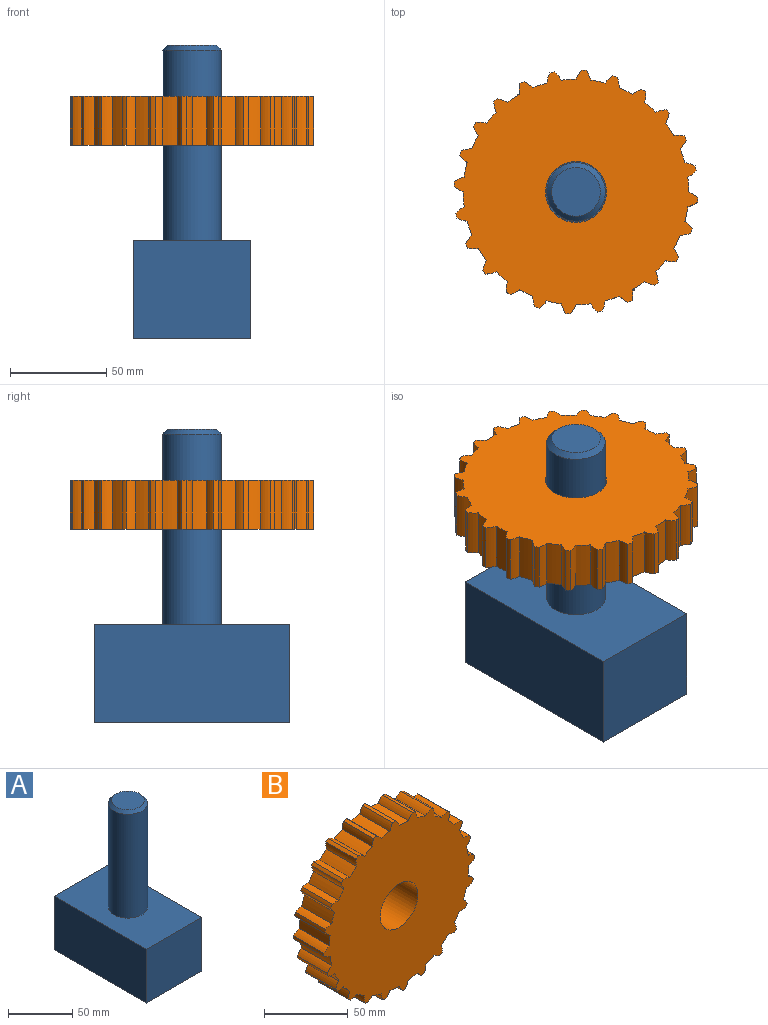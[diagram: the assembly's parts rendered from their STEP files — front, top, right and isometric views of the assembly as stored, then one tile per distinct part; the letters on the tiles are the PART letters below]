
ASSEMBLY  parts=2 mates=1
PART A: 9 faces, bbox 61.1x101.6x152.8 mm
  f0: plane 101.6x51.17mm, normal (1,0,0), area 5198.7mm2, adj f1,f3,f4,f5
  f1: plane 101.6x61.1mm, normal (0,0,1), area 5478.3mm2, adj f0,f2,f4,f5,f6
  f2: plane 101.6x51.17mm, normal (-1,0,0), area 5198.7mm2, adj f1,f3,f4,f5
  f3: plane 101.6x61.1mm, normal (0,0,-1), area 6207.9mm2, adj f0,f2,f4,f5
  f4: plane 61.1x51.17mm, normal (0,-1,0), area 3126.5mm2, adj f0,f1,f2,f3
  f5: plane 61.1x51.17mm, normal (0,1,0), area 3126.5mm2, adj f0,f1,f2,f3
  f6: cylinder r=15.24mm len=99.06mm, axis (0,0,-1), area 9485.6mm2, adj f1,f8
  f7: plane 25.4x25.4mm, normal (0,0,1), area 506.7mm2, adj f8
  f8: cone r=12.7mm half-angle=45deg, axis (0,0,-1), area 315.3mm2, adj f6,f7
PART B: 99 faces, bbox 126.7x25.4x126.7 mm
  f0: cylinder r=14.67mm len=25.4mm, axis (0,1,0), area 141.4mm2, adj f23,f26,f27,f28
  f1: cylinder r=58.67mm len=25.4mm, axis (0,1,0), area 195.1mm2, adj f27,f28,f68,f71
  f2: cylinder r=58.67mm len=25.4mm, axis (0,1,0), area 195.1mm2, adj f27,f28,f65,f67
  f3: cylinder r=58.67mm len=25.4mm, axis (0,1,0), area 195.1mm2, adj f27,f28,f62,f64
  f4: cylinder r=58.67mm len=25.4mm, axis (0,1,0), area 195.1mm2, adj f27,f28,f70,f74
  f5: cylinder r=58.67mm len=25.4mm, axis (0,1,0), area 195.1mm2, adj f27,f28,f73,f77
  f6: cylinder r=58.67mm len=25.4mm, axis (0,1,0), area 195.1mm2, adj f27,f28,f76,f80
  f7: cylinder r=58.67mm len=25.4mm, axis (0,1,0), area 195.1mm2, adj f27,f28,f79,f83
  f8: cylinder r=58.67mm len=25.4mm, axis (0,1,0), area 195.1mm2, adj f27,f28,f82,f86
  f9: cylinder r=58.67mm len=25.4mm, axis (0,1,0), area 195.1mm2, adj f27,f28,f85,f89
  f10: cylinder r=58.67mm len=25.4mm, axis (0,1,0), area 195.1mm2, adj f27,f28,f88,f92
  f11: cylinder r=58.67mm len=25.4mm, axis (0,1,0), area 195.1mm2, adj f27,f28,f91,f95
  f12: cylinder r=58.67mm len=25.4mm, axis (0,1,0), area 195.1mm2, adj f27,f28,f94,f96
  f13: cylinder r=58.67mm len=25.4mm, axis (0,1,0), area 195.1mm2, adj f27,f28,f35,f97
  f14: cylinder r=58.67mm len=25.4mm, axis (0,1,0), area 195.1mm2, adj f27,f28,f34,f38
  f15: cylinder r=58.67mm len=25.4mm, axis (0,1,0), area 195.1mm2, adj f27,f28,f37,f41
  f16: cylinder r=58.67mm len=25.4mm, axis (0,1,0), area 195.1mm2, adj f27,f28,f40,f44
  f17: cylinder r=58.67mm len=25.4mm, axis (0,1,0), area 195.1mm2, adj f27,f28,f43,f47
  f18: cylinder r=58.67mm len=25.4mm, axis (0,1,0), area 195.1mm2, adj f27,f28,f46,f50
  f19: cylinder r=58.67mm len=25.4mm, axis (0,1,0), area 195.1mm2, adj f27,f28,f49,f53
  f20: cylinder r=58.67mm len=25.4mm, axis (0,1,0), area 195.1mm2, adj f27,f28,f52,f56
  f21: cylinder r=58.67mm len=25.4mm, axis (0,1,0), area 195.1mm2, adj f27,f28,f55,f59
  f22: cylinder r=58.67mm len=25.4mm, axis (0,1,0), area 195.1mm2, adj f27,f28,f30,f58
  f23: cylinder r=58.67mm len=25.4mm, axis (0,1,0), area 195.1mm2, adj f0,f27,f28,f31
  f24: cylinder r=14.67mm len=25.4mm, axis (0,1,0), area 141.4mm2, adj f25,f26,f27,f28
  f25: cylinder r=58.67mm len=25.4mm, axis (0,1,0), area 195.1mm2, adj f24,f27,f28,f61
  f26: cylinder r=14.79mm len=25.4mm, axis (0,1,0), area 62.1mm2, adj f0,f24,f27,f28
  f27: plane 126.74x126.74mm, normal (0,-1,0), area 10648.5mm2, adj f0,f1,f2,f3,f4,f5,f6,f7
  f28: plane 126.74x126.74mm, normal (0,1,0), area 10648.5mm2, adj f0,f1,f2,f3,f4,f5,f6,f7
  f29: cylinder r=15.88mm len=31.75mm, axis (0,-1,0), area 2533.5mm2, adj f27,f28
  f30: cylinder r=14.67mm len=25.4mm, axis (0,1,0), area 141.4mm2, adj f22,f27,f28,f32
  f31: cylinder r=14.67mm len=25.4mm, axis (0,1,0), area 141.4mm2, adj f23,f27,f28,f32
  f32: cylinder r=14.79mm len=25.4mm, axis (0,1,0), area 62.1mm2, adj f27,f28,f30,f31
  f33: cylinder r=14.79mm len=25.4mm, axis (0,1,0), area 62.1mm2, adj f27,f28,f34,f35
  f34: cylinder r=14.67mm len=25.4mm, axis (0,1,0), area 141.4mm2, adj f14,f27,f28,f33
  f35: cylinder r=14.67mm len=25.4mm, axis (0,1,0), area 141.4mm2, adj f13,f27,f28,f33
  f36: cylinder r=14.79mm len=25.4mm, axis (0,1,0), area 62.1mm2, adj f27,f28,f37,f38
  f37: cylinder r=14.67mm len=25.4mm, axis (0,1,0), area 141.4mm2, adj f15,f27,f28,f36
  f38: cylinder r=14.67mm len=25.4mm, axis (0,1,0), area 141.4mm2, adj f14,f27,f28,f36
  f39: cylinder r=14.79mm len=25.4mm, axis (0,1,0), area 62.1mm2, adj f27,f28,f40,f41
  f40: cylinder r=14.67mm len=25.4mm, axis (0,1,0), area 141.4mm2, adj f16,f27,f28,f39
  f41: cylinder r=14.67mm len=25.4mm, axis (0,1,0), area 141.4mm2, adj f15,f27,f28,f39
  f42: cylinder r=14.79mm len=25.4mm, axis (0,1,0), area 62.1mm2, adj f27,f28,f43,f44
  f43: cylinder r=14.67mm len=25.4mm, axis (0,1,0), area 141.4mm2, adj f17,f27,f28,f42
  f44: cylinder r=14.67mm len=25.4mm, axis (0,1,0), area 141.4mm2, adj f16,f27,f28,f42
  f45: cylinder r=14.79mm len=25.4mm, axis (0,1,0), area 62.1mm2, adj f27,f28,f46,f47
  f46: cylinder r=14.67mm len=25.4mm, axis (0,1,0), area 141.4mm2, adj f18,f27,f28,f45
  f47: cylinder r=14.67mm len=25.4mm, axis (0,1,0), area 141.4mm2, adj f17,f27,f28,f45
  f48: cylinder r=14.79mm len=25.4mm, axis (0,1,0), area 62.1mm2, adj f27,f28,f49,f50
  f49: cylinder r=14.67mm len=25.4mm, axis (0,1,0), area 141.4mm2, adj f19,f27,f28,f48
  f50: cylinder r=14.67mm len=25.4mm, axis (0,1,0), area 141.4mm2, adj f18,f27,f28,f48
  f51: cylinder r=14.79mm len=25.4mm, axis (0,1,0), area 62.1mm2, adj f27,f28,f52,f53
  f52: cylinder r=14.67mm len=25.4mm, axis (0,1,0), area 141.4mm2, adj f20,f27,f28,f51
  f53: cylinder r=14.67mm len=25.4mm, axis (0,1,0), area 141.4mm2, adj f19,f27,f28,f51
  f54: cylinder r=14.79mm len=25.4mm, axis (0,1,0), area 62.1mm2, adj f27,f28,f55,f56
  f55: cylinder r=14.67mm len=25.4mm, axis (0,1,0), area 141.4mm2, adj f21,f27,f28,f54
  f56: cylinder r=14.67mm len=25.4mm, axis (0,1,0), area 141.4mm2, adj f20,f27,f28,f54
  f57: cylinder r=14.79mm len=25.4mm, axis (0,1,0), area 62.1mm2, adj f27,f28,f58,f59
  f58: cylinder r=14.67mm len=25.4mm, axis (0,1,0), area 141.4mm2, adj f22,f27,f28,f57
  f59: cylinder r=14.67mm len=25.4mm, axis (0,1,0), area 141.4mm2, adj f21,f27,f28,f57
  f60: cylinder r=14.79mm len=25.4mm, axis (0,1,0), area 62.1mm2, adj f27,f28,f61,f62
  f61: cylinder r=14.67mm len=25.4mm, axis (0,1,0), area 141.4mm2, adj f25,f27,f28,f60
  f62: cylinder r=14.67mm len=25.4mm, axis (0,1,0), area 141.4mm2, adj f3,f27,f28,f60
  f63: cylinder r=14.79mm len=25.4mm, axis (0,1,0), area 62.1mm2, adj f27,f28,f64,f65
  f64: cylinder r=14.67mm len=25.4mm, axis (0,1,0), area 141.4mm2, adj f3,f27,f28,f63
  f65: cylinder r=14.67mm len=25.4mm, axis (0,1,0), area 141.4mm2, adj f2,f27,f28,f63
  f66: cylinder r=14.79mm len=25.4mm, axis (0,1,0), area 62.1mm2, adj f27,f28,f67,f68
  f67: cylinder r=14.67mm len=25.4mm, axis (0,1,0), area 141.4mm2, adj f2,f27,f28,f66
  f68: cylinder r=14.67mm len=25.4mm, axis (0,1,0), area 141.4mm2, adj f1,f27,f28,f66
  f69: cylinder r=14.79mm len=25.4mm, axis (0,1,0), area 62.1mm2, adj f27,f28,f70,f71
  f70: cylinder r=14.67mm len=25.4mm, axis (0,1,0), area 141.4mm2, adj f4,f27,f28,f69
  f71: cylinder r=14.67mm len=25.4mm, axis (0,1,0), area 141.4mm2, adj f1,f27,f28,f69
  f72: cylinder r=14.79mm len=25.4mm, axis (0,1,0), area 62.1mm2, adj f27,f28,f73,f74
  f73: cylinder r=14.67mm len=25.4mm, axis (0,1,0), area 141.4mm2, adj f5,f27,f28,f72
  f74: cylinder r=14.67mm len=25.4mm, axis (0,1,0), area 141.4mm2, adj f4,f27,f28,f72
  f75: cylinder r=14.79mm len=25.4mm, axis (0,1,0), area 62.1mm2, adj f27,f28,f76,f77
  f76: cylinder r=14.67mm len=25.4mm, axis (0,1,0), area 141.4mm2, adj f6,f27,f28,f75
  f77: cylinder r=14.67mm len=25.4mm, axis (0,1,0), area 141.4mm2, adj f5,f27,f28,f75
  f78: cylinder r=14.79mm len=25.4mm, axis (0,1,0), area 62.1mm2, adj f27,f28,f79,f80
  f79: cylinder r=14.67mm len=25.4mm, axis (0,1,0), area 141.4mm2, adj f7,f27,f28,f78
  f80: cylinder r=14.67mm len=25.4mm, axis (0,1,0), area 141.4mm2, adj f6,f27,f28,f78
  f81: cylinder r=14.79mm len=25.4mm, axis (0,1,0), area 62.1mm2, adj f27,f28,f82,f83
  f82: cylinder r=14.67mm len=25.4mm, axis (0,1,0), area 141.4mm2, adj f8,f27,f28,f81
  f83: cylinder r=14.67mm len=25.4mm, axis (0,1,0), area 141.4mm2, adj f7,f27,f28,f81
  f84: cylinder r=14.79mm len=25.4mm, axis (0,1,0), area 62.1mm2, adj f27,f28,f85,f86
  f85: cylinder r=14.67mm len=25.4mm, axis (0,1,0), area 141.4mm2, adj f9,f27,f28,f84
  f86: cylinder r=14.67mm len=25.4mm, axis (0,1,0), area 141.4mm2, adj f8,f27,f28,f84
  f87: cylinder r=14.79mm len=25.4mm, axis (0,1,0), area 62.1mm2, adj f27,f28,f88,f89
  f88: cylinder r=14.67mm len=25.4mm, axis (0,1,0), area 141.4mm2, adj f10,f27,f28,f87
  f89: cylinder r=14.67mm len=25.4mm, axis (0,1,0), area 141.4mm2, adj f9,f27,f28,f87
  f90: cylinder r=14.79mm len=25.4mm, axis (0,1,0), area 62.1mm2, adj f27,f28,f91,f92
  f91: cylinder r=14.67mm len=25.4mm, axis (0,1,0), area 141.4mm2, adj f11,f27,f28,f90
  f92: cylinder r=14.67mm len=25.4mm, axis (0,1,0), area 141.4mm2, adj f10,f27,f28,f90
  f93: cylinder r=14.79mm len=25.4mm, axis (0,1,0), area 62.1mm2, adj f27,f28,f94,f95
  f94: cylinder r=14.67mm len=25.4mm, axis (0,1,0), area 141.4mm2, adj f12,f27,f28,f93
  f95: cylinder r=14.67mm len=25.4mm, axis (0,1,0), area 141.4mm2, adj f11,f27,f28,f93
  f96: cylinder r=14.67mm len=25.4mm, axis (0,1,0), area 141.4mm2, adj f12,f27,f28,f98
  f97: cylinder r=14.67mm len=25.4mm, axis (0,1,0), area 141.4mm2, adj f13,f27,f28,f98
  f98: cylinder r=14.79mm len=25.4mm, axis (0,1,0), area 62.1mm2, adj f27,f28,f96,f97
PLACE A t=(-63.99,-36.72,-89.02)mm
PLACE B rot(axis=(1,0,0),90deg) t=(-67.04,-87.52,2.68)mm
MATE revolute B.f1 <-> A.f8  axis (0,0,-1) through (-67.04,-87.52,-10.02)mm
